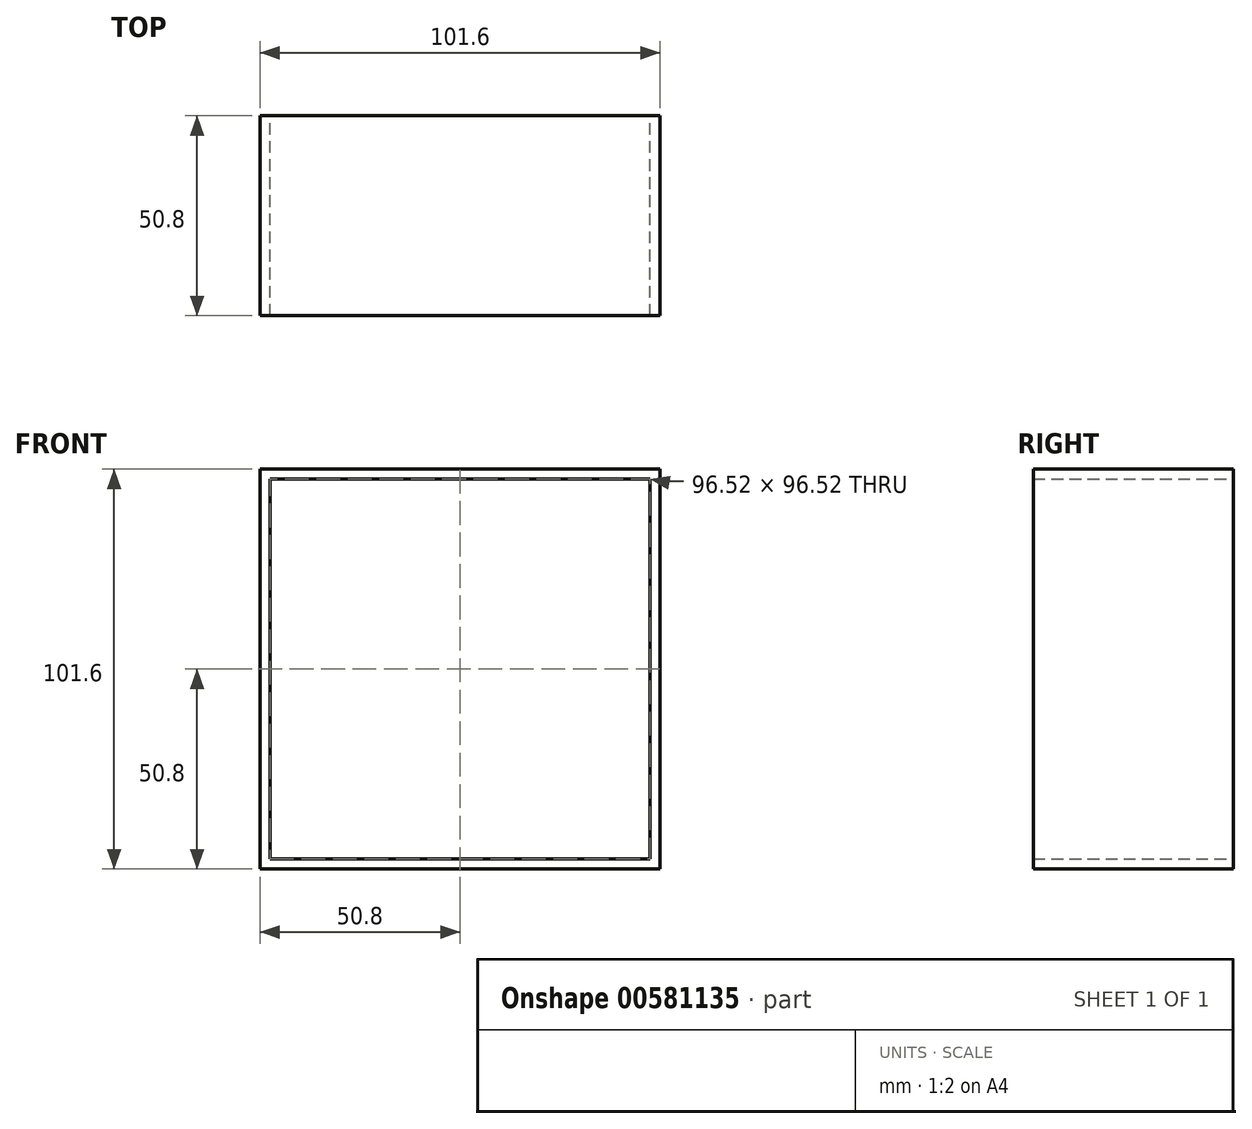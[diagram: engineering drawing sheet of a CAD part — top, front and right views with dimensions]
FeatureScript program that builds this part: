
annotation { "Feature Type Name" : "Feature", "Feature Type Description" : "" }
export const myFeature = defineFeature(function(context is Context, id is Id, definition is map)
    precondition{}
    {
        {
            var Q0;
            Q0=qCreatedBy(makeId("Front.planeOp"),FACE);
            var sketch = newSketch(context, id + "F0", { "sketchPlane" : qUnion([Q0])});
            skLineSegment(sketch, "E0", {"start": v(0, 83.7) * mm, "end": v(0, -66.88) * mm, "construction": true});
            skLineSegment(sketch, "E1", {"start": v(-60.12, 0) * mm, "end": v(72.18, 0) * mm, "construction": true});
            skLineSegment(sketch, "E2", {"start": v(-50.8, 50.8) * mm, "end": v(50.8, 50.8) * mm});
            skLineSegment(sketch, "E3", {"start": v(50.8, 50.8) * mm, "end": v(50.8, -50.8) * mm});
            skLineSegment(sketch, "E4", {"start": v(50.8, -50.8) * mm, "end": v(-50.8, -50.8) * mm});
            skLineSegment(sketch, "E5", {"start": v(-50.8, -50.8) * mm, "end": v(-50.8, 50.8) * mm});
            skSolve(sketch);
        }
        {
            var Q0;
            Q0 = qSketchRegion(id + "F0", true);
            extrude(context, id + "F1", {"entities" : qUnion([Q0]), "depth" : 50.8 * mm, "offsetDistance" : 25.4 * mm});
        }
        {
            var Q0;
            Q0=makeQuery(id+"F1.opExtrude","CAP_FACE",FACE,{"disambiguationData":[OSD([sQuery(id+"F0.wireOp",EDGE,"E2"),sQuery(id+"F0.wireOp",EDGE,"E3"),sQuery(id+"F0.wireOp",EDGE,"E4"),sQuery(id+"F0.wireOp",EDGE,"E5")])],"isStart":false});
            var Q1;
            Q1=makeQuery(id+"F1.opExtrude","CAP_FACE",FACE,{"disambiguationData":[OSD([sQuery(id+"F0.wireOp",EDGE,"E2"),sQuery(id+"F0.wireOp",EDGE,"E3"),sQuery(id+"F0.wireOp",EDGE,"E4"),sQuery(id+"F0.wireOp",EDGE,"E5")])],"isStart":true});
            shell(context, id + "F2", {"entities" : qUnion([Q0, Q1]), "thickness" : 2.54 * mm});
        }
    });
